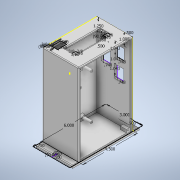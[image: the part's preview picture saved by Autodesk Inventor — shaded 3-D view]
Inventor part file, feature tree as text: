
AUTODESK INVENTOR PART (.ipt)
format: ipt  version: 2020 (Build 240168000, 168)  size: 4,372,992 bytes
history: native  units: in
note: dims shown in document units (in); Inventor stores cm internally (conversion verified against a paired STEP export)
features: sketch x24, extrude x17, hole x5, fillet x3, revolve x3, helix x3, thread x2, pattern_linear x2, other x1
ambient origin geometry x8: Origin, YZ Plane, XZ Plane, XY Plane, X Axis, Y Axis, Z Axis, Center Point
bodies: Solid1 (feature_tree), Solid3 (feature_tree), Solid4 (feature_tree), Solid5 (feature_tree)
feature tree (60):
  sketch  "Sketch1"  dims[d0=3.0in d1=6.0in]
  extrude  "Extrusion1"  Depth=6.0in
  extrude  "Extrusion2"  Depth=4.5in
  hole  "Hole1"  [1 undecoded]
  extrude  "Extrusion7"  Depth=0.1875in
  extrude  "Extrusion8"  Depth=0.1875in
  extrude  "Extrusion3"  Depth=0.125in
  extrude  "Extrusion4"  Depth=0.125in
  extrude  "Extrusion5"  Depth=0.125in TaperAngle=0.0deg
  extrude  "Extrusion6"  Depth=0.25in
  extrude  "Extrusion9"  Depth=0.5in
  hole  "Hole2"  [1 undecoded]
  thread  "Thread1"  [1 undecoded]
  pattern_linear  "Rectangular Pattern1"  Count1=2 Spacing1=1.9291in
  extrude  "Extrusion10"  Depth=0.3937in
  sketch  "Sketch13"  dims[d32=0.25in d33=0.25in d34=0.0in d35=0.5906in]
  hole  "Hole5"  [1 undecoded]
  thread  "Thread3"  [1 undecoded]
  pattern_linear  "Rectangular Pattern2"  Spacing1=0.1875in  [1 undecoded]
  hole  "Hole4"  [1 undecoded]
  fillet  "Fillet1"  Radius=0.125in
  extrude  "Extrusion11"  Depth=0.125in
  extrude  "Extrusion12"  Depth=0.3937in
  sketch  "Sketch18"  dims[d38=2.2835in]
  extrude  "Extrusion13"  Depth=0.3937in
  hole  "Hole6"  [1 undecoded]
  fillet  "Fillet2"  Radius=0.841in
  other  "iFeature13:2"
  sketch  "Sketch20"  dims[d41=0.5in]
  extrude  "Extrusion14"  Depth=0.3937in
  extrude  "Extrusion15"  Depth=0.3937in
  sketch  "Sketch21"  dims[d42=90.0deg]
  extrude  "Extrusion16"  TaperAngle=0.0deg  [1 undecoded]
  extrude  "Extrusion17"  Depth=0.3937in
  fillet  "Fillet3"  Radius=3.0in
  revolve  "Revolution2"  [1 undecoded]
  helix  "Coil2"  [1 undecoded]
  revolve  "Revolution3"  [1 undecoded]
  helix  "Coil3"  [1 undecoded]
  revolve  "Revolution4"  [1 undecoded]
  helix  "Coil4"  [1 undecoded]
  sketch  "Sketch2"  dims[d2=0.75in d3=4.5in]
  sketch  "Sketch3"  dims[d4=0.1875in d5=0.0in d6=6.75in d7=0.0in]
  sketch  "Sketch4"  dims[d8=0.5in]
  sketch  "Sketch5"  dims[d9=0.266in d10=0.75in d11=0.507in d12=0.0625in d13=0.5635in d14=1.0in d15=0.8108in d16=0.1875in]
  sketch  "Sketch6"  dims[d17=0.1875in d18=0.1875in]
  sketch  "Sketch7"  dims[d19=2.8125in d20=0.0in d21=0.125in]
  sketch  "Sketch8"  dims[d22=0.125in d23=0.125in]
  sketch  "Sketch9"  dims[d24=0.125in d25=0.125in d26=0.0in]
  sketch  "Sketch10"  dims[d27=0.5in d28=0.25in]
  sketch  "Sketch12"  dims[d29=0.25in d30=0.0in d31=0.5in]
  sketch  "Sketch16"  dims[d36=0.3937in]
  sketch  "Sketch17"  dims[d37=1.9291in]
  sketch  "Sketch19"  dims[d39=0.25in d40=0.0in]
  sketch  "Sketch24"  dims[d43=0.25in d44=0.0in]
  sketch  "Sketch25"  dims[d45=0.1969in]
  sketch  "Sketch26"  dims[d46=0.25in d47=0.0in]
  sketch  "Sketch27"  dims[d48=0.0807in d49=0.197in d50=0.119in d51=0.188in d52=90.0deg d53=0.25in d54=0.8108in]
  sketch  "Sketch28"  dims[d55=0.25in d56=0.0in d57=0.7874in d59=1.9291in]
  sketch  "Sketch29"  dims[d60=0.7874in d62=2.2835in d63=0.4035in d65=0.8406in d66=0.0in d76=0.7874in d78=2.6772in d79=0.7874in d81=3.6614in d82=0.1875in d83=0.1875in d84=0.125in d85=0.125in d86=0.089in d87=0.146in d88=0.119in d89=0.188in d90=0.5635in d91=0.224in d92=0.8108in d93=0.0625in d94=0.0492in d95=0.1969in d96=0.0807in d97=0.197in d98=0.119in d99=0.188in d100=0.5635in d101=0.259in d102=0.8108in d103=0.841in d104=0.0in d128=2.75in d130=1.5in d131=0.0in d132=1.0in d133=3.0in d134=0.0625in d135=0.0in d136=1.5in d137=0.5in d138=90.0deg d139=0.75in d140=2.75in d141=0.125in d142=0.0in d143=0.375in d144=0.375in d145=0.375in d146=0.375in d147=0.375in d148=0.0in d149=0.1875in d150=0.1875in d151=0.1875in d152=0.1875in d153=0.089in d154=0.197in d155=0.119in d156=0.188in d157=0.5635in d158=0.259in d159=0.8108in d160=0.0625in d161=0.12in d163=0.492in d165=0.129in d167=0.04in d173=1.25in d174=0.75in d175=90.0deg d176=0.4724in d177=0.375in d178=0.0in d179=0.5in d180=1.0in d181=0.748in d182=1.043in d183=0.5in d184=0.748in d185=1.043in d186=0.0197in d187=0.0in d188=0.375in d189=90.0deg d190=0.25in d191=90.0deg d192=0.5in d193=0.75in d194=0.25in d195=0.0in d196=0.0197in d197=0.0in d198=0.125in d206=0.3779in d217=0.3779in d218=0.0028in d219=0.0028in d222=0.0177in d224=0.3779in d226=0.0in d227=0.0177in d228=0.2854in d229=0.3937in d230=0.0in d231=0.0in d232=0.0in d233=0.0in d234=0.0in d235=0.748in d236=1.043in d237=0.3779in d238=0.0028in d239=0.0028in d242=0.0177in d244=0.3779in d246=0.0in d247=0.0177in d248=0.2854in d249=0.3937in d250=0.0in d251=0.0in d252=0.0in d253=0.0in d254=0.0in d255=0.3779in d256=0.0028in d257=0.0028in d260=0.0177in d262=0.3779in d264=0.0in d265=0.0177in d266=0.876in d267=0.3937in d268=0.0in d269=0.0in d270=0.0in d271=0.0in d272=0.0in]
note: 15 required parameter values undecoded (feature->parameter linkage not recoverable at this tier; creation-order binding heuristic only, values carry confidence <= 0.55)